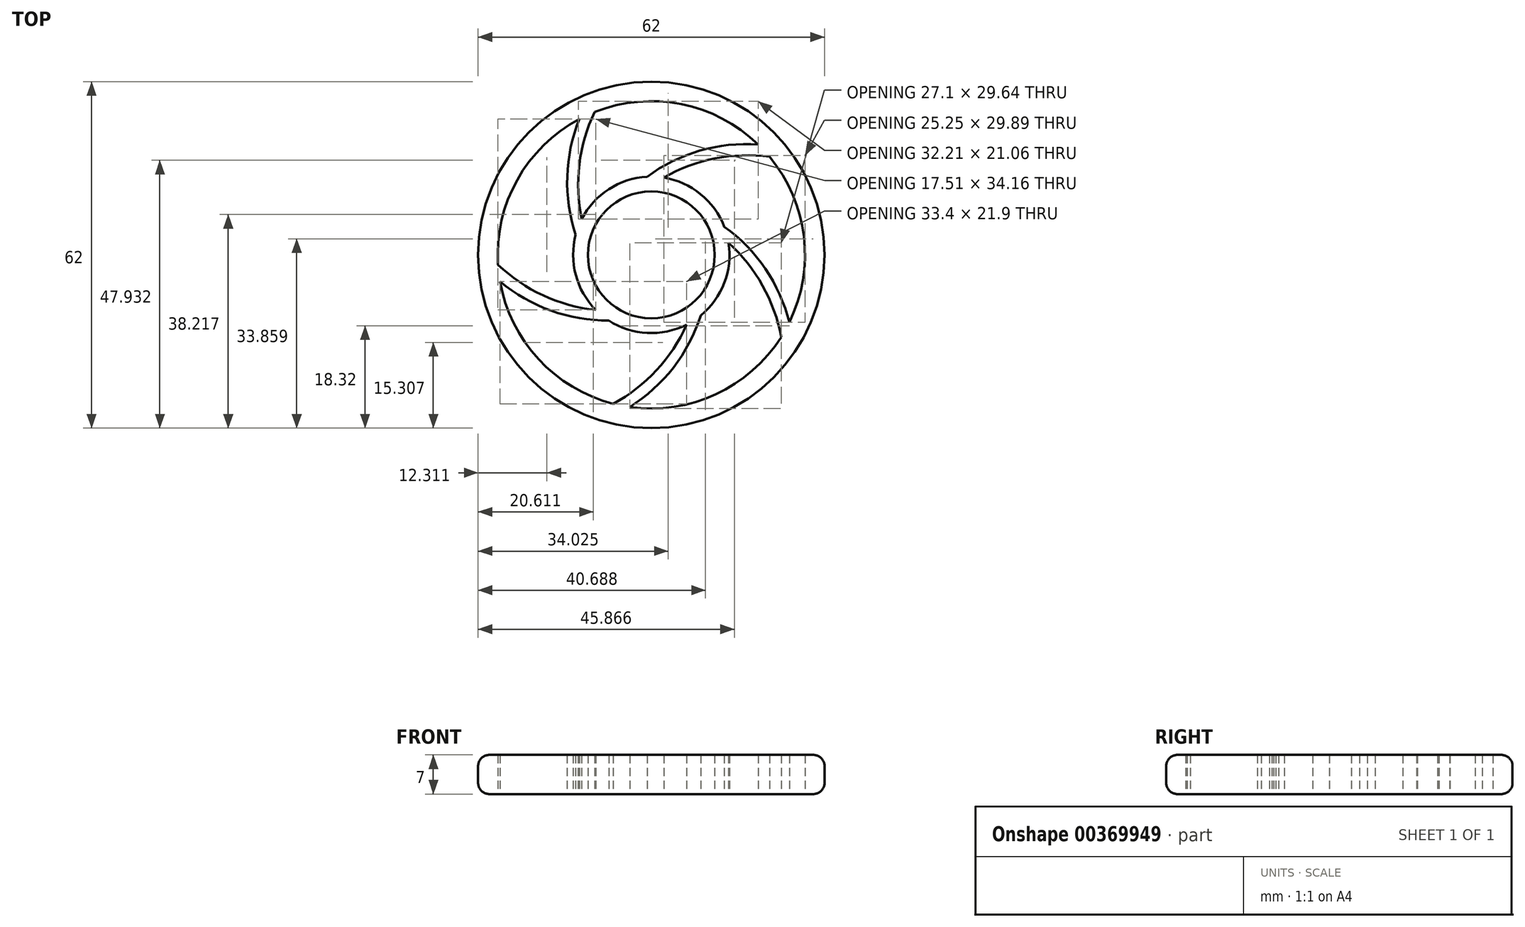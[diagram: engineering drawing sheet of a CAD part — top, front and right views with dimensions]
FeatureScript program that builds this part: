
annotation { "Feature Type Name" : "Feature", "Feature Type Description" : "" }
export const myFeature = defineFeature(function(context is Context, id is Id, definition is map)
    precondition{}
    {
        {
            var Q0;
            Q0=qCreatedBy(makeId("Top.planeOp"),FACE);
            var sketch = newSketch(context, id + "F0", { "sketchPlane" : qUnion([Q0])});
            skCircle(sketch, "E0", {"center": v(0, 0) * mm, "radius": 11.35 * mm});
            skCircle(sketch, "E1", {"center": v(0, 0) * mm, "radius": 27.5 * mm});
            skCircle(sketch, "E2", {"center": v(0, 0) * mm, "radius": 31 * mm});
            skCircle(sketch, "E3", {"center": v(0, 0) * mm, "radius": 14 * mm});
            skArc(sketch, "E4", {"start": v(21.17, 17.56) * mm, "mid": v(11.4, 17.25) * mm, "end": v(2.24, 13.82) * mm});
            skArc(sketch, "E5", {"start": v(19.13, 19.76) * mm, "mid": v(8.67, 18.64) * mm, "end": v(-0.76, 13.98) * mm});
            skArc(sketch, "E6.1.1", {"start": v(-10.16, 25.56) * mm, "mid": v(-12.89, 16.17) * mm, "end": v(-12.45, 6.4) * mm});
            skArc(sketch, "E6.1.2", {"start": v(-12.88, 24.3) * mm, "mid": v(-15.05, 14) * mm, "end": v(-13.53, 3.6) * mm});
            skArc(sketch, "E6.2.1", {"start": v(-27.44, -1.76) * mm, "mid": v(-19.36, -7.26) * mm, "end": v(-9.93, -9.86) * mm});
            skArc(sketch, "E6.2.2", {"start": v(-27.09, -4.74) * mm, "mid": v(-17.97, -9.98) * mm, "end": v(-7.6, -11.75) * mm});
            skArc(sketch, "E6.3.1", {"start": v(-6.8, -26.64) * mm, "mid": v(0.92, -20.65) * mm, "end": v(6.31, -12.5) * mm});
            skArc(sketch, "E6.3.2", {"start": v(-3.86, -27.23) * mm, "mid": v(3.94, -20.18) * mm, "end": v(8.83, -10.87) * mm});
            skArc(sketch, "E6.4.1", {"start": v(23.24, -14.7) * mm, "mid": v(19.93, -5.5) * mm, "end": v(13.84, 2.14) * mm});
            skArc(sketch, "E6.4.2", {"start": v(24.7, -12.09) * mm, "mid": v(20.4, -2.49) * mm, "end": v(13.06, 5.04) * mm});
            skSolve(sketch);
        }
        {
            var Q0;
            {var subQ0=sQuery(id+"F0.wireOp",EDGE,"E6.8.1");Q0=makeQuery(id+"F0.imprint","IMPRINT",FACE,{"disambiguationData":[TD([[makeQuery(id+"F0.imprint","IMPRINT",EDGE,{"derivedFrom":subQ0}),-1.0]])]});}
            var Q1;
            Q1=makeQuery(id+"F0.imprint","IMPRINT",FACE,{"disambiguationData":[TD([[makeQuery(id+"F0.imprint","IMPRINT",EDGE,{"derivedFrom":sQuery(id+"F0.wireOp",EDGE,"E0")}),-1.0]])]});
            var Q2;
            {var subQ0=sQuery(id+"F0.wireOp",EDGE,"E6.6.1");Q2=makeQuery(id+"F0.imprint","IMPRINT",FACE,{"disambiguationData":[TD([[makeQuery(id+"F0.imprint","IMPRINT",EDGE,{"derivedFrom":subQ0}),-1.0]])]});}
            var Q3;
            {var subQ0=sQuery(id+"F0.wireOp",EDGE,"E6.5.1");Q3=makeQuery(id+"F0.imprint","IMPRINT",FACE,{"disambiguationData":[TD([[makeQuery(id+"F0.imprint","IMPRINT",EDGE,{"derivedFrom":subQ0}),-1.0]])]});}
            var Q4;
            {var subQ0=sQuery(id+"F0.wireOp",EDGE,"E6.9.1");Q4=makeQuery(id+"F0.imprint","IMPRINT",FACE,{"disambiguationData":[TD([[makeQuery(id+"F0.imprint","IMPRINT",EDGE,{"derivedFrom":subQ0}),-1.0]])]});}
            var Q5;
            {var subQ0=sQuery(id+"F0.wireOp",EDGE,"E4");Q5=makeQuery(id+"F0.imprint","IMPRINT",FACE,{"disambiguationData":[TD([[makeQuery(id+"F0.imprint","IMPRINT",EDGE,{"derivedFrom":subQ0}),-1.0]])]});}
            var Q6;
            {var subQ0=sQuery(id+"F0.wireOp",EDGE,"E6.1.1");Q6=makeQuery(id+"F0.imprint","IMPRINT",FACE,{"disambiguationData":[TD([[makeQuery(id+"F0.imprint","IMPRINT",EDGE,{"derivedFrom":subQ0}),-1.0]])]});}
            var Q7;
            {var subQ0=sQuery(id+"F0.wireOp",EDGE,"E6.2.1");Q7=makeQuery(id+"F0.imprint","IMPRINT",FACE,{"disambiguationData":[TD([[makeQuery(id+"F0.imprint","IMPRINT",EDGE,{"derivedFrom":subQ0}),-1.0]])]});}
            var Q8;
            {var subQ0=sQuery(id+"F0.wireOp",EDGE,"E6.3.1");Q8=makeQuery(id+"F0.imprint","IMPRINT",FACE,{"disambiguationData":[TD([[makeQuery(id+"F0.imprint","IMPRINT",EDGE,{"derivedFrom":subQ0}),-1.0]])]});}
            var Q9;
            {var subQ0=sQuery(id+"F0.wireOp",EDGE,"E6.4.1");Q9=makeQuery(id+"F0.imprint","IMPRINT",FACE,{"disambiguationData":[TD([[makeQuery(id+"F0.imprint","IMPRINT",EDGE,{"derivedFrom":subQ0}),-1.0]])]});}
            var Q10;
            Q10=makeQuery(id+"F0.imprint","IMPRINT",FACE,{"disambiguationData":[TD([[makeQuery(id+"F0.imprint","IMPRINT",EDGE,{"derivedFrom":sQuery(id+"F0.wireOp",EDGE,"E2")}),1.0]])]});
            var Q11;
            {var subQ0=sQuery(id+"F0.wireOp",EDGE,"E6.7.1");Q11=makeQuery(id+"F0.imprint","IMPRINT",FACE,{"disambiguationData":[TD([[makeQuery(id+"F0.imprint","IMPRINT",EDGE,{"derivedFrom":subQ0}),-1.0]])]});}
            extrude(context, id + "F1", {"entities" : qUnion([Q0, Q1, Q2, Q3, Q4, Q5, Q6, Q7, Q8, Q9, Q10, Q11]), "depth" : 7 * mm, "offsetDistance" : 25 * mm});
        }
        {
            var Q0;
            Q0=makeQuery(id+"F1.opExtrude","CAP_EDGE",EDGE,{"disambiguationData":[OSD([sQuery(id+"F0.wireOp",EDGE,"E2")])],"isStart":false});
            var Q1;
            Q1=makeQuery(id+"F1.opExtrude","CAP_EDGE",EDGE,{"disambiguationData":[OSD([sQuery(id+"F0.wireOp",EDGE,"E2")])],"isStart":true});
            fillet(context, id + "F2", {"entities" : qUnion([Q0, Q1]), "radius" : 2 * mm, "tangentPropagation" : true, "allowEdgeOverflow" : false});
        }
    });
